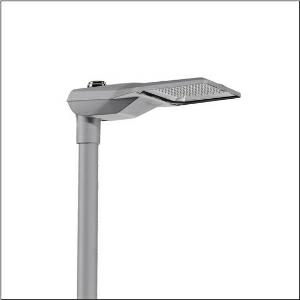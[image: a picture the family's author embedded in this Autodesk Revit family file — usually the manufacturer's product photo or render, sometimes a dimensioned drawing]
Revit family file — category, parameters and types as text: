
# Revit family: streetlight_sl_21_midi___pl52_5xe7h47n08mb_5c45
name_source: partatom
category: Lighting Fixtures
units: mm (PartAtom-declared; Revit-internal decimal feet)

## family parameters
Cut with Voids When Loaded = No
Host = Face
Light Source = No
Part Type = Normal
Room Calculation Point = No
Round Connector Dimension = Use Diameter
Shared = No

## types (1)
- --- (1 x LED, 19830 lm, 147 W, 4000K)
    Apparent Load = 147 VA
    CIE Flux Codes = 27 59 98 100 100
    Color Rendering = 70
    Color Temperature = 4000K
    Default Elevation = 1800 mm
    Description = Streetlight SL 21 midi, mast luminaire, primary light control with lens, of PMMA, primary optical cover: cover, of toughened safety glass, transparent, light distribution: PL52, light emission: direct distribution, primary light characteristic: asymmetric, installation type: side-entry, LED, 3G 2.5mm², High Power LED, rated luminous flux: 19.830lm, luminous efficacy: 135lm/W, light colour: 740, colour temperature: 4000K, control gear: NEMA (7pin), control: overheat protection, pre-setting: linear dimming characteristic, constant luminous flux control, time-dependent luminous flux control, flexible luminous flux parameterisation, mains connection: 220..240V, AC, 50/60Hz, connection cable pre-assembled, cable length: 12,5m, wiring characteristics: H05VV-F, start of lifetime: 147W, end of service life: 155W, reduction: 65W, luminaire housing, of diecast aluminium (EN AC-44300), powder-coated, SITECO metallic grey (DB 702S), corrosivity category C5 high according to DIN EN ISO 12944, multi-level sealing system, sealing non-destructively replaceable, inclination adjustable: 0°, 5°, 10°, 15°, length: 644mm, width: 335mm, height: 110mm, spigot size: 42mm (side-entry), mounting height: 4..8m, protection rating (complete): IP66, insulation class (complete): insulation class I (protective earthing), certification: CE, ENEC, ENEC+, VDE, impact resistance: IK10, permissible operating ambient temperature for outdoor applications: -40..+50°C, standard-compliant lighting for roads and squares, packaging unit: 1 piece

Light Distribution: PL52
    Height = 111 mm
    Lamp = 1 x LED
    Lamp Light Flux = 19830 lm
    Lamp Power = 147 W
    Lamp count = 1
    Length = 644 mm
    Luminous efficacy = 135 lm/W
    Manufacturer = Siteco
    ModVariant = No
    Model = 5XE7H47N08MB
    Number of Poles = 1
    OnlyDefault = Yes
    Power Factor = 1
    Product Name = Streetlight SL 21 midi | PL52
    Product group = mast luminaire | pylon top
    ProductGroupID = 6100
    Protection Class = Protection class I
    Protection Degree = IP 66
    RLX_Detail_Level = 1
    RLX_Emergency_Light_Flux = 0 lm
    RLX_Emergency_Type = 0
    RLX_Emergency_Type_DB = No
    RlxData = <blob elided: 36177 chars, md5=ee06088a>
    Socket = socket
    Standby Power = 0 W
    System Light Flux = 19830 lm
    System Power = 147 W
    Type Comments = factory setting: luminous flux: 100 % | dim-lin: 254 | 750 mA
    Type Image = l_1294377.jpg
    URL = http://relux.com
    VarID = @adj_136305
    Voltage = 0 V
    Weight = 0.00 kg
    Width = 336 mm

## geometry (parser evidence)
native form markers: Blend x4, Sweep x11
no freeform markers — native parametric forms only
